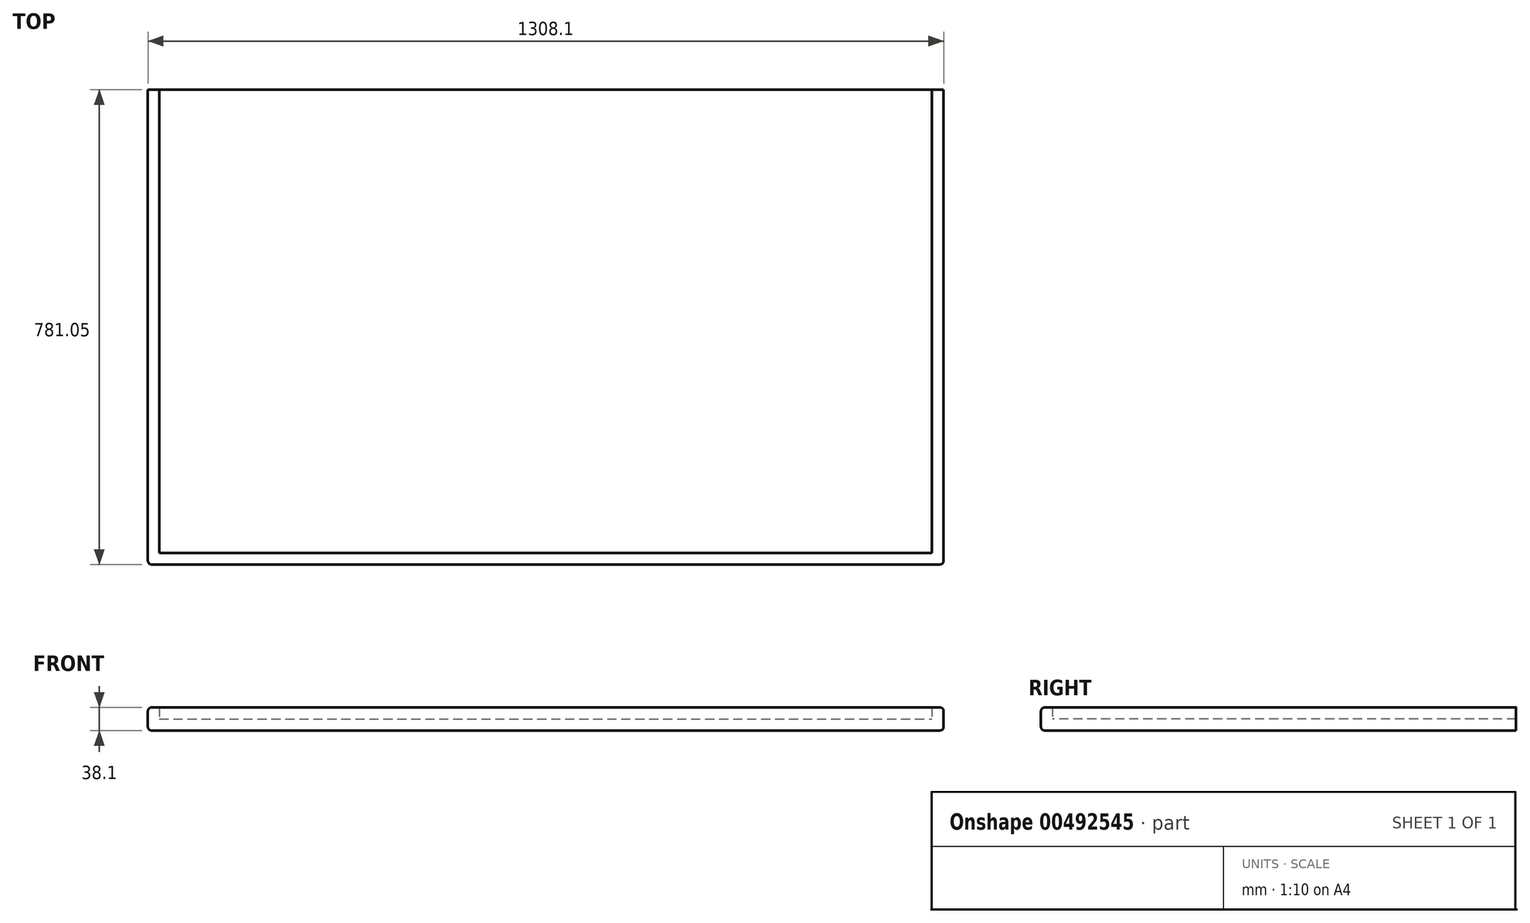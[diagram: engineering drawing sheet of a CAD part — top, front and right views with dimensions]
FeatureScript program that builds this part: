
annotation { "Feature Type Name" : "Feature", "Feature Type Description" : "" }
export const myFeature = defineFeature(function(context is Context, id is Id, definition is map)
    precondition{}
    {
        {
            var Q0;
            Q0=qCreatedBy(makeId("Top.planeOp"),FACE);
            var sketch = newSketch(context, id + "F0", { "sketchPlane" : qUnion([Q0])});
            skLineSegment(sketch, "E0.bottom", {"start": v(-689.06, 465.64) * mm, "end": v(580.94, 465.64) * mm});
            skLineSegment(sketch, "E0.top", {"start": v(-689.06, -296.36) * mm, "end": v(580.94, -296.36) * mm});
            skLineSegment(sketch, "E0.left", {"start": v(-689.06, 465.64) * mm, "end": v(-689.06, -296.36) * mm});
            skLineSegment(sketch, "E0.right", {"start": v(580.94, 465.64) * mm, "end": v(580.94, -296.36) * mm});
            skLineSegment(sketch, "E1.bottom", {"start": v(-689.06, 465.64) * mm, "end": v(-708.11, 465.64) * mm});
            skLineSegment(sketch, "E1.top", {"start": v(-689.06, -315.4) * mm, "end": v(-708.11, -315.4) * mm});
            skLineSegment(sketch, "E1.left", {"start": v(-689.06, 465.64) * mm, "end": v(-689.06, -315.4) * mm});
            skLineSegment(sketch, "E1.right", {"start": v(-708.11, 465.64) * mm, "end": v(-708.11, -315.4) * mm});
            skLineSegment(sketch, "E2.bottom", {"start": v(-689.06, -315.4) * mm, "end": v(580.94, -315.4) * mm});
            skLineSegment(sketch, "E2.left", {"start": v(-689.06, -315.4) * mm, "end": v(-689.06, -296.36) * mm});
            skLineSegment(sketch, "E2.right", {"start": v(580.94, -315.4) * mm, "end": v(580.94, -296.36) * mm});
            skLineSegment(sketch, "E3.bottom", {"start": v(580.94, 465.64) * mm, "end": v(599.99, 465.64) * mm});
            skLineSegment(sketch, "E3.top", {"start": v(580.94, -315.4) * mm, "end": v(599.99, -315.4) * mm});
            skLineSegment(sketch, "E3.left", {"start": v(580.94, 465.64) * mm, "end": v(580.94, -315.4) * mm});
            skLineSegment(sketch, "E3.right", {"start": v(599.99, 465.64) * mm, "end": v(599.99, -315.4) * mm});
            skSolve(sketch);
        }
        {
            var Q0;
            {var subQ0=sQuery(id+"F0.wireOp",EDGE,"E0.bottom");Q0=makeQuery(id+"F0.imprint","IMPRINT",FACE,{"disambiguationData":[TD([[makeQuery(id+"F0.imprint","IMPRINT",EDGE,{"derivedFrom":subQ0}),-1.0]])]});}
            extrude(context, id + "F1", {"entities" : qUnion([Q0]), "depth" : 19.05 * mm});
        }
        {
            var Q0;
            Q0=makeQuery(id+"F0.imprint","IMPRINT",FACE,{"disambiguationData":[TD([[makeQuery(id+"F0.imprint","IMPRINT",EDGE,{"derivedFrom":sQuery(id+"F0.wireOp",EDGE,"E1.bottom")}),1.0]])]});
            var Q1;
            {var subQ0=sQuery(id+"F0.wireOp",EDGE,"E2.bottom");Q1=makeQuery(id+"F0.imprint","IMPRINT",FACE,{"disambiguationData":[TD([[makeQuery(id+"F0.imprint","IMPRINT",EDGE,{"derivedFrom":subQ0}),1.0]])]});}
            var Q2;
            {var subQ3=sQuery(id+"F0.wireOp",EDGE,"E3.bottom");Q2=makeQuery(id+"F0.imprint","IMPRINT",FACE,{"disambiguationData":[TD([[makeQuery(id+"F0.imprint","IMPRINT",EDGE,{"derivedFrom":subQ3}),-1.0]])]});}
            extrude(context, id + "F2", {"entities" : qUnion([Q0, Q1, Q2]), "operationType" : NewBodyOperationType.ADD, "depth" : 38.1 * mm});
        }
        {
            var Q0;
            Q0=makeQuery(id+"F2.opExtrude","CAP_EDGE",EDGE,{"disambiguationData":[OSD([sQuery(id+"F0.wireOp",EDGE,"E3.right")])],"isStart":true});
            var Q1;
            Q1=makeQuery(id+"F2.opExtrude","CAP_EDGE",EDGE,{"disambiguationData":[OSD([sQuery(id+"F0.wireOp",EDGE,"E1.top"),sQuery(id+"F0.wireOp",EDGE,"E2.bottom"),sQuery(id+"F0.wireOp",EDGE,"E3.top")])],"isStart":true});
            var Q2;
            Q2=makeQuery(id+"F2.opExtrude","CAP_EDGE",EDGE,{"disambiguationData":[OSD([sQuery(id+"F0.wireOp",EDGE,"E1.right")])],"isStart":true});
            var Q3;
            Q3=makeQuery(id+"F2.opExtrude","CAP_EDGE",EDGE,{"disambiguationData":[OSD([sQuery(id+"F0.wireOp",EDGE,"E1.right")])],"isStart":false});
            var Q4;
            Q4=makeQuery(id+"F2.opExtrude","SWEPT_EDGE",EDGE,{"disambiguationData":[OSD([sQuery(id+"F0.wireOp",EDGE,"E1.top"),sQuery(id+"F0.wireOp",EDGE,"E1.right")])]});
            var Q5;
            Q5=makeQuery(id+"F2.opExtrude","CAP_EDGE",EDGE,{"disambiguationData":[OSD([sQuery(id+"F0.wireOp",EDGE,"E1.top"),sQuery(id+"F0.wireOp",EDGE,"E2.bottom"),sQuery(id+"F0.wireOp",EDGE,"E3.top")])],"isStart":false});
            var Q6;
            Q6=makeQuery(id+"F2.opExtrude","CAP_EDGE",EDGE,{"disambiguationData":[OSD([sQuery(id+"F0.wireOp",EDGE,"E3.right")])],"isStart":false});
            var Q7;
            Q7=makeQuery(id+"F2.opExtrude","SWEPT_EDGE",EDGE,{"disambiguationData":[OSD([sQuery(id+"F0.wireOp",EDGE,"E3.top"),sQuery(id+"F0.wireOp",EDGE,"E3.right")])]});
            fillet(context, id + "F3", {"entities" : qUnion([Q0, Q1, Q2, Q3, Q4, Q5, Q6, Q7]), "radius" : 6.35 * mm, "tangentPropagation" : true, "allowEdgeOverflow" : false});
        }
    });
